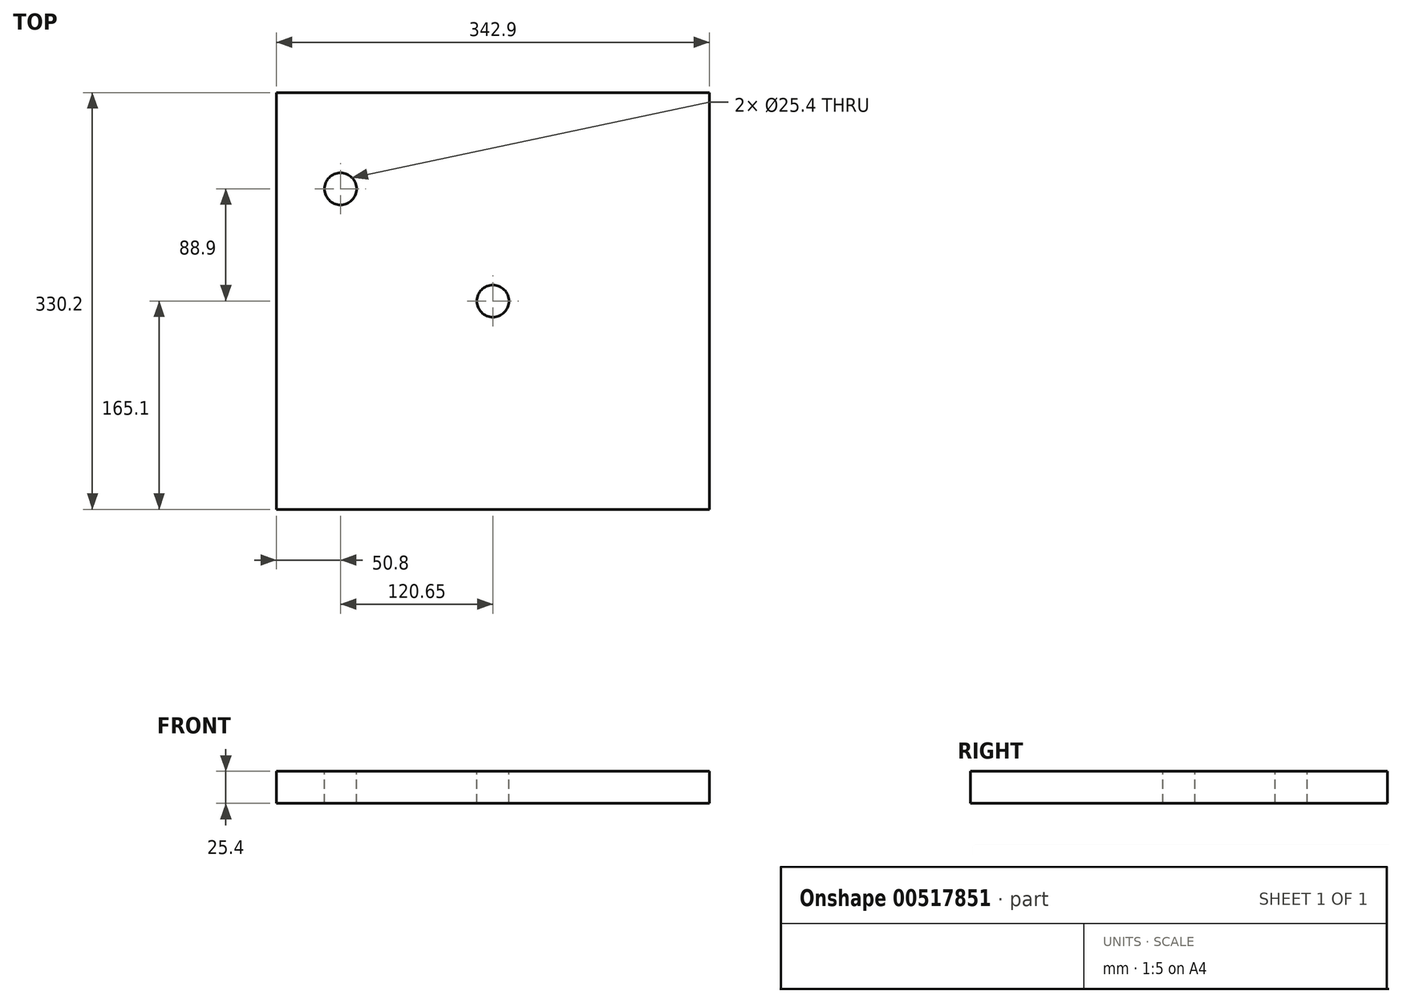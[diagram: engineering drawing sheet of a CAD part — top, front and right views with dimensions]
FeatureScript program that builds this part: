
annotation { "Feature Type Name" : "Feature", "Feature Type Description" : "" }
export const myFeature = defineFeature(function(context is Context, id is Id, definition is map)
    precondition{}
    {
        {
            var Q0;
            Q0=qCreatedBy(makeId("Top.planeOp"),FACE);
            var sketch = newSketch(context, id + "F0", { "sketchPlane" : qUnion([Q0])});
            skLineSegment(sketch, "E0.bottom", {"start": v(0, 330.2) * mm, "end": v(342.9, 330.2) * mm});
            skLineSegment(sketch, "E0.top", {"start": v(0, 0) * mm, "end": v(342.9, 0) * mm});
            skLineSegment(sketch, "E0.left", {"start": v(0, 330.2) * mm, "end": v(0, 0) * mm});
            skLineSegment(sketch, "E0.right", {"start": v(342.9, 330.2) * mm, "end": v(342.9, 0) * mm});
            skSolve(sketch);
        }
        {
            var Q0;
            Q0 = qSketchRegion(id + "F0", true);
            extrude(context, id + "F1", {"entities" : qUnion([Q0]), "depth" : 25.4 * mm, "offsetDistance" : 25.4 * mm});
        }
        {
            var Q0;
            Q0=makeQuery(id+"F1.opExtrude","CAP_FACE",FACE,{"disambiguationData":[OSD([sQuery(id+"F0.wireOp",EDGE,"E0.bottom"),sQuery(id+"F0.wireOp",EDGE,"E0.top"),sQuery(id+"F0.wireOp",EDGE,"E0.left"),sQuery(id+"F0.wireOp",EDGE,"E0.right")])],"isStart":false});
            var sketch = newSketch(context, id + "F2", { "sketchPlane" : qUnion([Q0])});
            skCircle(sketch, "E1", {"center": v(50.8, 254) * mm, "radius": 12.7 * mm});
            skSolve(sketch);
        }
        {
            var Q0;
            Q0 = qSketchRegion(id + "F2", true);
            extrude(context, id + "F3", {"entities" : qUnion([Q0]), "operationType" : NewBodyOperationType.REMOVE, "endBound" : BoundingType.THROUGH_ALL, "oppositeDirection" : true, "depth" : 25.4 * mm, "offsetDistance" : 25.4 * mm});
        }
        {
            var Q0;
            Q0=makeQuery(id+"F1.opExtrude","CAP_FACE",FACE,{"disambiguationData":[OSD([sQuery(id+"F0.wireOp",EDGE,"E0.bottom"),sQuery(id+"F0.wireOp",EDGE,"E0.top"),sQuery(id+"F0.wireOp",EDGE,"E0.left"),sQuery(id+"F0.wireOp",EDGE,"E0.right")])],"isStart":false});
            var sketch = newSketch(context, id + "F4", { "sketchPlane" : qUnion([Q0])});
            skCircle(sketch, "E2", {"center": v(171.45, 165.1) * mm, "radius": 12.7 * mm});
            skSolve(sketch);
        }
        {
            var Q0;
            Q0 = qSketchRegion(id + "F4", true);
            extrude(context, id + "F5", {"entities" : qUnion([Q0]), "operationType" : NewBodyOperationType.REMOVE, "endBound" : BoundingType.THROUGH_ALL, "oppositeDirection" : true, "depth" : 25.4 * mm, "offsetDistance" : 25.4 * mm});
        }
    });
